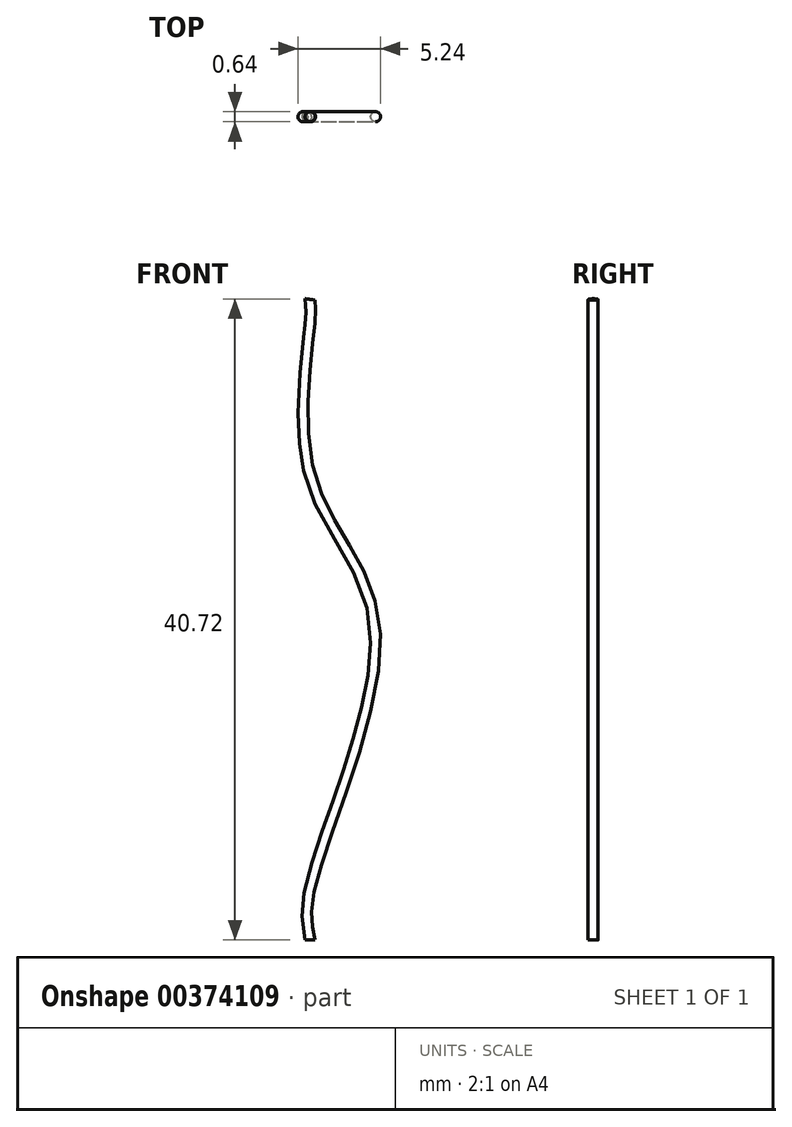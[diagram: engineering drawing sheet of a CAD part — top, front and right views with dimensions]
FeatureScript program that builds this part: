
annotation { "Feature Type Name" : "Feature", "Feature Type Description" : "" }
export const myFeature = defineFeature(function(context is Context, id is Id, definition is map)
    precondition{}
    {
        {
            var Q0;
            Q0=qCreatedBy(makeId("Top.planeOp"),FACE);
            var sketch = newSketch(context, id + "F0", { "sketchPlane" : qUnion([Q0])});
            skCircle(sketch, "E0", {"center": v(0, 0) * mm, "radius": 0.32 * mm});
            skSolve(sketch);
        }
        {
            var Q0;
            Q0=qCreatedBy(makeId("Front.planeOp"),FACE);
            var sketch = newSketch(context, id + "F1", { "sketchPlane" : qUnion([Q0])});
            skFitSpline(sketch, "E1", {"points": [v(0, 0) * mm, v(0, 3.34) * mm, v(4.13, 19.73) * mm, v(0, 29.46) * mm, v(0, 39.25) * mm, v(0, 40.68) * mm], "startDerivative": vector(-4.15, 18.87) * mm, "endDerivative": vector(-1.03, 11.88) * mm});
            skSolve(sketch);
        }
        {
            var Q0;
            Q0=makeQuery(id+"F0.imprint","IMPRINT",FACE,{"disambiguationData":[TD([[makeQuery(id+"F0.imprint","IMPRINT",EDGE,{"derivedFrom":sQuery(id+"F0.wireOp",EDGE,"E0")}),1.0]])]});
            var Q1;
            Q1=sQuery(id+"F1.wireOp",EDGE,"E1");
            sweep(context, id + "F2", {"profiles" : qUnion([Q0]), "path" : qUnion([Q1])});
        }
    });
